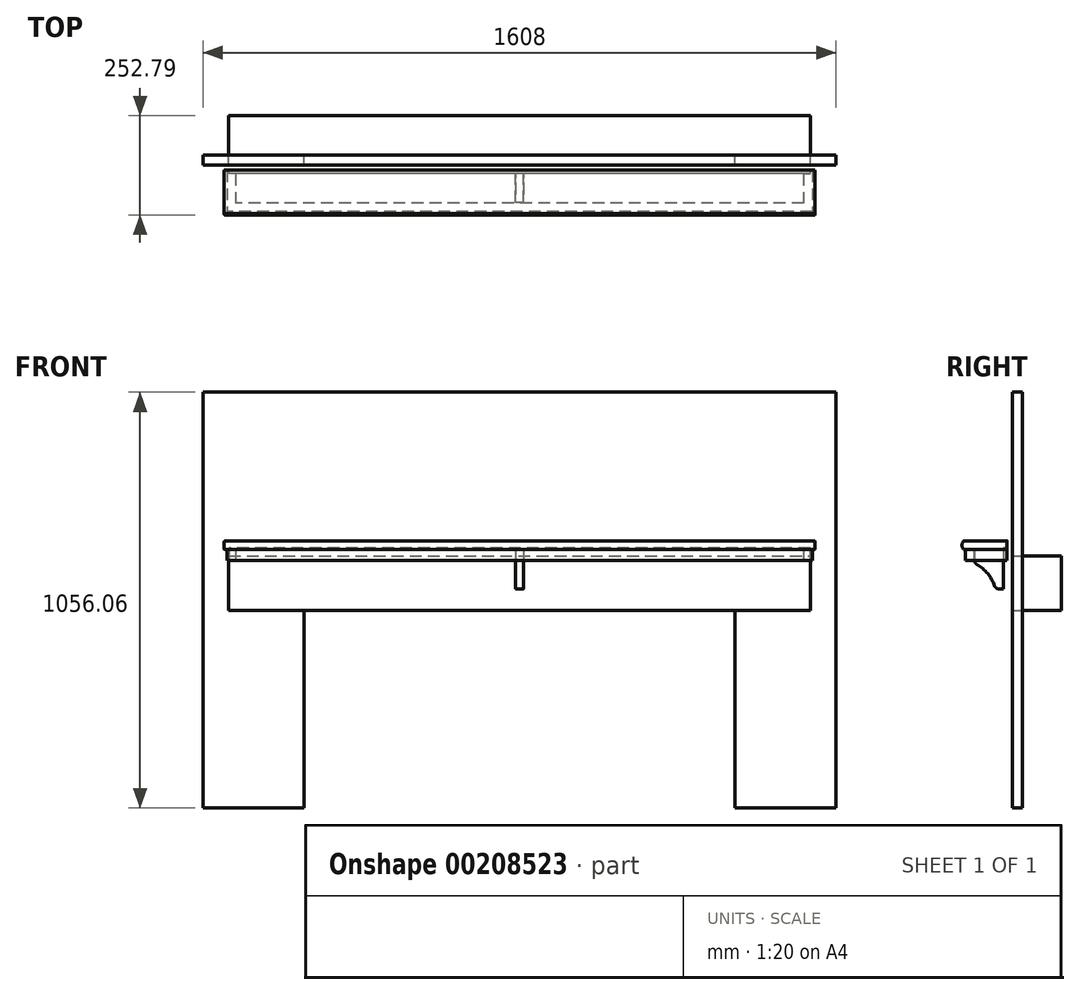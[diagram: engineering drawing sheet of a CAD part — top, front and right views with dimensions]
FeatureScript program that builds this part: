
annotation { "Feature Type Name" : "Feature", "Feature Type Description" : "" }
export const myFeature = defineFeature(function(context is Context, id is Id, definition is map)
    precondition{}
    {
        {
            var Q0;
            Q0=qCreatedBy(makeId("Front.planeOp"),FACE);
            var sketch = newSketch(context, id + "F0", { "sketchPlane" : qUnion([Q0])});
            skLineSegment(sketch, "E0.bottom", {"start": v(-739, 0) * mm, "end": v(739, 0) * mm});
            skLineSegment(sketch, "E0.top", {"start": v(-739, 138) * mm, "end": v(739, 138) * mm});
            skLineSegment(sketch, "E0.left", {"start": v(-739, 0) * mm, "end": v(-739, 138) * mm});
            skLineSegment(sketch, "E0.right", {"start": v(739, 0) * mm, "end": v(739, 138) * mm});
            skSolve(sketch);
        }
        {
            var Q0;
            Q0 = qSketchRegion(id + "F0", true);
            extrude(context, id + "F1", {"entities" : qUnion([Q0]), "oppositeDirection" : true, "depth" : 100 * mm});
        }
        {
            var Q0;
            Q0=qCreatedBy(makeId("Right.planeOp"),FACE);
            var sketch = newSketch(context, id + "F2", { "sketchPlane" : qUnion([Q0])});
            skLineSegment(sketch, "E1", {"start": v(-38.79, 176.13) * mm, "end": v(-148.79, 176.13) * mm});
            skLineSegment(sketch, "E2", {"start": v(-11.55, 165.13) * mm, "end": v(-291.73, 165.13) * mm, "construction": true});
            skLineSegment(sketch, "E3", {"start": v(-148.79, 176.13) * mm, "end": v(-148.79, 154.13) * mm, "construction": true});
            skPoint(sketch, "E4", {"position": v(-148.79, 165.13) * mm});
            skArc(sketch, "E5", {"start": v(-148.79, 176.13) * mm, "mid": v(-152.79, 165.13) * mm, "end": v(-148.79, 154.13) * mm});
            skLineSegment(sketch, "E6", {"start": v(-152.79, 183.06) * mm, "end": v(-152.79, 134.02) * mm, "construction": true});
            skLineSegment(sketch, "E7", {"start": v(-38.79, 176.13) * mm, "end": v(-38.79, 158.13) * mm});
            skLineSegment(sketch, "E8", {"start": v(-38.79, 158.13) * mm, "end": v(-47.79, 158.13) * mm});
            skLineSegment(sketch, "E9", {"start": v(-47.79, 158.13) * mm, "end": v(-47.79, 154.13) * mm});
            skLineSegment(sketch, "E10", {"start": v(-148.79, 154.13) * mm, "end": v(-47.79, 154.13) * mm});
            skSolve(sketch);
        }
        {
            var Q0;
            Q0 = qSketchRegion(id + "F2", true);
            extrude(context, id + "F3", {"entities" : qUnion([Q0]), "endBound" : BoundingType.SYMMETRIC, "depth" : 1501 * mm});
        }
        {
            var Q0;
            Q0=makeQuery(id+"F3.opExtrude","CAP_FACE",FACE,{"disambiguationData":[OSD([sQuery(id+"F2.wireOp",EDGE,"E1"),sQuery(id+"F2.wireOp",EDGE,"E5"),sQuery(id+"F2.wireOp",EDGE,"E7"),sQuery(id+"F2.wireOp",EDGE,"E8"),sQuery(id+"F2.wireOp",EDGE,"E9"),sQuery(id+"F2.wireOp",EDGE,"E10")])],"isStart":false});
            var sketch = newSketch(context, id + "F4", { "sketchPlane" : qUnion([Q0])});
            skLineSegment(sketch, "E11.0", {"start": v(-38.79, 158.13) * mm, "end": v(-47.79, 158.13) * mm});
            skLineSegment(sketch, "E11.1", {"start": v(-47.79, 158.13) * mm, "end": v(-47.79, 154.13) * mm});
            skLineSegment(sketch, "E12", {"start": v(-47.79, 154.13) * mm, "end": v(-38.79, 154.13) * mm});
            skLineSegment(sketch, "E13", {"start": v(-38.79, 154.13) * mm, "end": v(-38.79, 158.13) * mm});
            skSolve(sketch);
        }
        {
            var Q0;
            Q0 = qSketchRegion(id + "F4", true);
            extrude(context, id + "F5", {"entities" : qUnion([Q0]), "operationType" : NewBodyOperationType.ADD, "oppositeDirection" : true, "depth" : 12 * mm});
        }
        {
            var Q0;
            Q0=makeQuery(id+"F3.opExtrude","CAP_FACE",FACE,{"disambiguationData":[OSD([sQuery(id+"F2.wireOp",EDGE,"E1"),sQuery(id+"F2.wireOp",EDGE,"E5"),sQuery(id+"F2.wireOp",EDGE,"E7"),sQuery(id+"F2.wireOp",EDGE,"E8"),sQuery(id+"F2.wireOp",EDGE,"E9"),sQuery(id+"F2.wireOp",EDGE,"E10")])],"isStart":true});
            var sketch = newSketch(context, id + "F6", { "sketchPlane" : qUnion([Q0])});
            skLineSegment(sketch, "E14.0", {"start": v(38.79, 158.13) * mm, "end": v(47.79, 158.13) * mm});
            skLineSegment(sketch, "E14.1", {"start": v(47.79, 158.13) * mm, "end": v(47.79, 154.13) * mm});
            skLineSegment(sketch, "E15", {"start": v(47.79, 154.13) * mm, "end": v(38.79, 154.13) * mm});
            skLineSegment(sketch, "E16", {"start": v(38.79, 158.13) * mm, "end": v(38.79, 154.13) * mm});
            skSolve(sketch);
        }
        {
            var Q0;
            Q0 = qSketchRegion(id + "F6", true);
            extrude(context, id + "F7", {"entities" : qUnion([Q0]), "operationType" : NewBodyOperationType.ADD, "oppositeDirection" : true, "depth" : 12 * mm});
        }
        {
            var Q0;
            Q0=makeQuery(id+"F3.opExtrude","CAP_EDGE",EDGE,{"disambiguationData":[OSD([sQuery(id+"F2.wireOp",EDGE,"E10")])],"isStart":false});
            var Q1;
            Q1=makeQuery(id+"F3.opExtrude","CAP_EDGE",EDGE,{"disambiguationData":[OSD([sQuery(id+"F2.wireOp",EDGE,"E5")])],"isStart":false});
            var Q2;
            Q2=makeQuery(id+"F3.opExtrude","CAP_EDGE",EDGE,{"disambiguationData":[OSD([sQuery(id+"F2.wireOp",EDGE,"E1")])],"isStart":false});
            var Q3;
            Q3=makeQuery(id+"F3.opExtrude","CAP_EDGE",EDGE,{"disambiguationData":[OSD([sQuery(id+"F2.wireOp",EDGE,"E5")])],"isStart":true});
            var Q4;
            Q4=makeQuery(id+"F3.opExtrude","CAP_EDGE",EDGE,{"disambiguationData":[OSD([sQuery(id+"F2.wireOp",EDGE,"E10")])],"isStart":true});
            var Q5;
            Q5=makeQuery(id+"F3.opExtrude","CAP_EDGE",EDGE,{"disambiguationData":[OSD([sQuery(id+"F2.wireOp",EDGE,"E1")])],"isStart":true});
            fillet(context, id + "F8", {"entities" : qUnion([Q0, Q1, Q2, Q3, Q4, Q5]), "radius" : 2 * mm, "tangentPropagation" : true, "allowEdgeOverflow" : false});
        }
        {
            var Q0;
            Q0=qCreatedBy(makeId("Right.planeOp"),FACE);
            var sketch = newSketch(context, id + "F9", { "sketchPlane" : qUnion([Q0])});
            skLineSegment(sketch, "E17.bottom", {"start": v(6.08, 193.84) * mm, "end": v(56.08, 193.84) * mm});
            skLineSegment(sketch, "E17.top", {"start": v(6.08, 143.84) * mm, "end": v(56.08, 143.84) * mm});
            skLineSegment(sketch, "E17.left", {"start": v(6.08, 193.84) * mm, "end": v(6.08, 143.84) * mm});
            skLineSegment(sketch, "E17.right", {"start": v(56.08, 193.84) * mm, "end": v(56.08, 143.84) * mm});
            skSolve(sketch);
        }
        {
            var Q0;
            Q0=makeQuery(id+"F3.opExtrude","SWEPT_FACE",FACE,{"disambiguationData":[OSD([sQuery(id+"F2.wireOp",EDGE,"E10")])]});
            var sketch = newSketch(context, id + "F10", { "sketchPlane" : qUnion([Q0])});
            skLineSegment(sketch, "E18", {"start": v(743.5, 38.79) * mm, "end": v(743.5, 143.79) * mm});
            skLineSegment(sketch, "E19", {"start": v(743.5, 143.79) * mm, "end": v(-743.5, 143.79) * mm});
            skLineSegment(sketch, "E20", {"start": v(743.5, 38.79) * mm, "end": v(721.5, 38.79) * mm});
            skLineSegment(sketch, "E21", {"start": v(721.5, 38.79) * mm, "end": v(721.5, 121.79) * mm});
            skLineSegment(sketch, "E22", {"start": v(721.5, 121.79) * mm, "end": v(-721.5, 121.79) * mm});
            skLineSegment(sketch, "E23", {"start": v(0, 0) * mm, "end": v(0, 256.93) * mm, "construction": true});
            skLineSegment(sketch, "E24.MirrorCS", {"start": v(-721.5, 38.79) * mm, "end": v(-721.5, 121.79) * mm});
            skLineSegment(sketch, "E25.MirrorCS", {"start": v(-743.5, 38.79) * mm, "end": v(-743.5, 143.79) * mm});
            skLineSegment(sketch, "E26.MirrorCS", {"start": v(-743.5, 38.79) * mm, "end": v(-721.5, 38.79) * mm});
            skSolve(sketch);
        }
        {
            var Q0;
            Q0 = qSketchRegion(id + "F10", true);
            extrude(context, id + "F11", {"entities" : qUnion([Q0]), "operationType" : NewBodyOperationType.ADD, "depth" : (28) * mm});
        }
        {
            var Q0;
            Q0=qCreatedBy(makeId("Right.planeOp"),FACE);
            var sketch = newSketch(context, id + "F12", { "sketchPlane" : qUnion([Q0])});
            skLineSegment(sketch, "E27", {"start": v(-120.79, 154.13) * mm, "end": v(-47.79, 154.13) * mm});
            skLineSegment(sketch, "E28", {"start": v(-47.79, 154.13) * mm, "end": v(-47.79, 54.13) * mm});
            skLineSegment(sketch, "E29", {"start": v(-47.79, 54.13) * mm, "end": v(-67.79, 54.13) * mm});
            skLineSegment(sketch, "E30", {"start": v(-120.79, 154.13) * mm, "end": v(-120.79, 119.13) * mm});
            skLineSegment(sketch, "E31", {"start": v(-120.79, 119.13) * mm, "end": v(-67.79, 54.13) * mm, "construction": true});
            skArc(sketch, "E32", {"start": v(-67.79, 54.13) * mm, "mid": v(-87.15, 92.46) * mm, "end": v(-120.79, 119.13) * mm});
            skLineSegment(sketch, "E33", {"start": v(-94.29, 86.63) * mm, "end": v(-192.94, 6.2) * mm, "construction": true});
            skSolve(sketch);
        }
        {
            var Q0;
            Q0 = qSketchRegion(id + "F12", true);
            extrude(context, id + "F13", {"entities" : qUnion([Q0]), "endBound" : BoundingType.SYMMETRIC, "depth" : 20 * mm});
        }
        {
            var Q0;
            Q0=qCreatedBy(makeId("Front.planeOp"),FACE);
            var sketch = newSketch(context, id + "F14", { "sketchPlane" : qUnion([Q0])});
            skLineSegment(sketch, "E34.0", {"start": v(-739, 0) * mm, "end": v(-739, 138) * mm, "construction": true});
            skLineSegment(sketch, "E34.1", {"start": v(-739, 0) * mm, "end": v(739, 0) * mm, "construction": true});
            skLineSegment(sketch, "E34.2", {"start": v(-739, 138) * mm, "end": v(739, 138) * mm, "construction": true});
            skLineSegment(sketch, "E34.3", {"start": v(739, 0) * mm, "end": v(739, 138) * mm, "construction": true});
            skLineSegment(sketch, "E35", {"start": v(-547, 0) * mm, "end": v(-547, -502.17) * mm});
            skLineSegment(sketch, "E36", {"start": v(-804, 553.9) * mm, "end": v(-804, -502.17) * mm});
            skLineSegment(sketch, "E37", {"start": v(0, -215.37) * mm, "end": v(0, 384.48) * mm, "construction": true});
            skLineSegment(sketch, "E38.MirrorCS", {"start": v(804, 553.9) * mm, "end": v(804, -502.17) * mm});
            skLineSegment(sketch, "E39.MirrorCS", {"start": v(547, 0) * mm, "end": v(547, -502.17) * mm});
            skLineSegment(sketch, "E40", {"start": v(-804, 553.9) * mm, "end": v(804, 553.9) * mm});
            skLineSegment(sketch, "E41", {"start": v(-804, -502.17) * mm, "end": v(-547, -502.17) * mm});
            skLineSegment(sketch, "E42", {"start": v(547, -502.17) * mm, "end": v(804, -502.17) * mm});
            skLineSegment(sketch, "E43", {"start": v(-547, 0) * mm, "end": v(-739, 0) * mm});
            skLineSegment(sketch, "E44", {"start": v(-739, 138) * mm, "end": v(739, 138) * mm});
            skLineSegment(sketch, "E45", {"start": v(739, 0) * mm, "end": v(547, 0) * mm});
            skLineSegment(sketch, "E46", {"start": v(547, 0) * mm, "end": v(739, 0) * mm});
            skLineSegment(sketch, "E47", {"start": v(739, 138) * mm, "end": v(-739, 138) * mm});
            skLineSegment(sketch, "E48", {"start": v(-739, 138) * mm, "end": v(-739, 0) * mm});
            skLineSegment(sketch, "E49", {"start": v(-739, 0) * mm, "end": v(-547, 0) * mm});
            skLineSegment(sketch, "E50", {"start": v(739, 138) * mm, "end": v(739, 0) * mm});
            skSolve(sketch);
        }
        {
            var Q0;
            Q0 = qSketchRegion(id + "F14", true);
            extrude(context, id + "F15", {"entities" : qUnion([Q0]), "depth" : 25 * mm});
        }
        {
            var Q0;
            Q0=makeQuery(id+"F11.boolean.opBoolean","MERGE",FACE,{"derivedFrom":[makeQuery(id+"F7.boolean.opBoolean","MERGE",FACE,{"derivedFrom":[makeQuery(id+"F5.boolean.opBoolean","MERGE",FACE,{"derivedFrom":[makeQuery(id+"F3.opExtrude","SWEPT_FACE",FACE,{"disambiguationData":[OSD([sQuery(id+"F2.wireOp",EDGE,"E7")])]}),makeQuery(id+"F5.opExtrude","SWEPT_FACE",FACE,{"disambiguationData":[OSD([sQuery(id+"F4.wireOp",EDGE,"E13")])]})]}),makeQuery(id+"F7.opExtrude","SWEPT_FACE",FACE,{"disambiguationData":[OSD([sQuery(id+"F6.wireOp",EDGE,"E16")])]})]}),makeQuery(id+"F11.opExtrude","SWEPT_FACE",FACE,{"disambiguationData":[OSD([sQuery(id+"F10.wireOp",EDGE,"E20")])]}),makeQuery(id+"F11.opExtrude","SWEPT_FACE",FACE,{"disambiguationData":[OSD([sQuery(id+"F10.wireOp",EDGE,"E26.MirrorCS")])]})]});
            var sketch = newSketch(context, id + "F16", { "sketchPlane" : qUnion([Q0])});
            skLineSegment(sketch, "E51.bottom", {"start": v(-738.5, 154.13) * mm, "end": v(-721.5, 154.13) * mm});
            skLineSegment(sketch, "E51.top", {"start": v(-738.5, 126.13) * mm, "end": v(-721.5, 126.13) * mm});
            skLineSegment(sketch, "E51.left", {"start": v(-738.5, 154.13) * mm, "end": v(-738.5, 126.13) * mm});
            skLineSegment(sketch, "E51.right", {"start": v(-721.5, 154.13) * mm, "end": v(-721.5, 126.13) * mm});
            skLineSegment(sketch, "E52.bottom", {"start": v(738.5, 154.13) * mm, "end": v(721.5, 154.13) * mm});
            skLineSegment(sketch, "E52.top", {"start": v(738.5, 126.13) * mm, "end": v(721.5, 126.13) * mm});
            skLineSegment(sketch, "E52.left", {"start": v(738.5, 154.13) * mm, "end": v(738.5, 126.13) * mm});
            skLineSegment(sketch, "E52.right", {"start": v(721.5, 154.13) * mm, "end": v(721.5, 126.13) * mm});
            skSolve(sketch);
        }
        {
            var Q0;
            Q0 = qSketchRegion(id + "F16", true);
            var Q1;
            Q1=makeQuery(id+"F3.opExtrude","SWEPT_FACE",FACE,{"disambiguationData":[OSD([sQuery(id+"F2.wireOp",EDGE,"E9")])]});
            extrude(context, id + "F17", {"entities" : qUnion([Q0]), "operationType" : NewBodyOperationType.REMOVE, "endBound" : BoundingType.UP_TO_SURFACE, "oppositeDirection" : true, "endBoundEntityFace" : qUnion([Q1]), "depth" : 25 * mm});
        }
        {
            var Q0;
            Q0=makeQuery(id+"F13.opExtrude","SWEPT_EDGE",EDGE,{"disambiguationData":[OSD([sQuery(id+"F12.wireOp",EDGE,"E30"),sQuery(id+"F12.wireOp",EDGE,"E32")])]});
            var Q1;
            Q1=makeQuery(id+"F13.opExtrude","SWEPT_EDGE",EDGE,{"disambiguationData":[OSD([sQuery(id+"F12.wireOp",EDGE,"E29"),sQuery(id+"F12.wireOp",EDGE,"E32")])]});
            fillet(context, id + "F18", {"entities" : qUnion([Q0, Q1]), "radius" : 12 * mm, "tangentPropagation" : true, "allowEdgeOverflow" : false});
        }
    });
